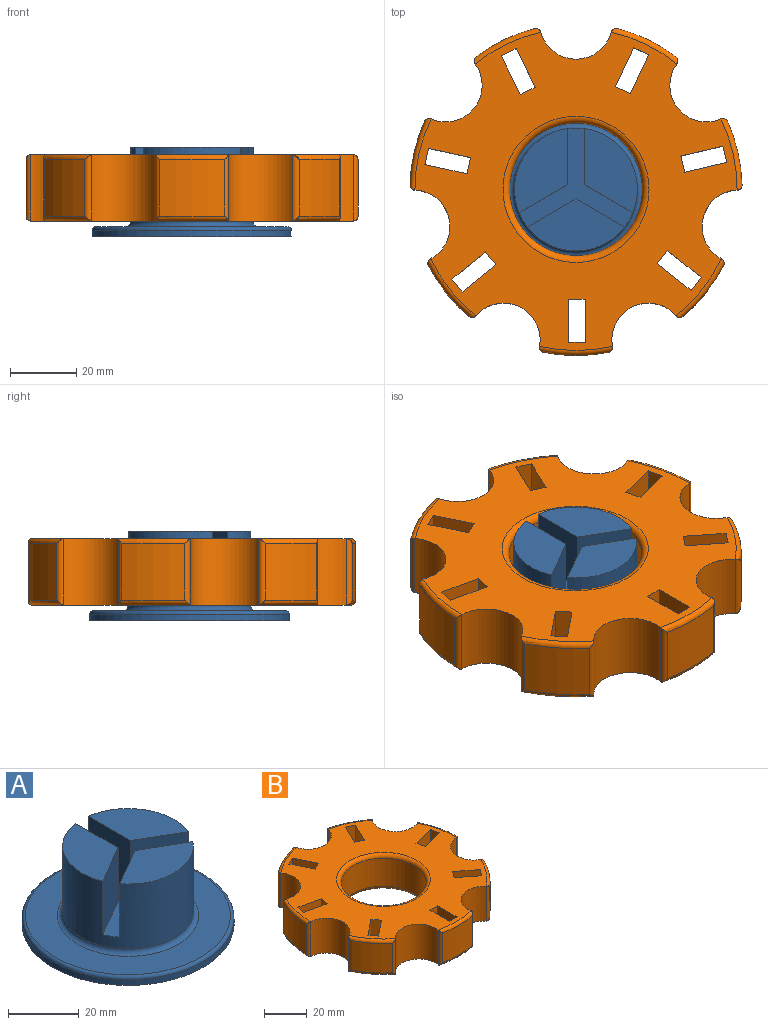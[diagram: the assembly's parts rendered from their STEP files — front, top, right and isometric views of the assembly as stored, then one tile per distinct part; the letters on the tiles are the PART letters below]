
ASSEMBLY  parts=2 mates=1
PART A: 16 faces, bbox 64.9x64.9x27 mm
  f0: plane 29.25x15.61mm, normal (0,0,1), area 269.8mm2, adj f3,f7,f8
  f1: plane 25.33x16mm, normal (0,0,1), area 269.8mm2, adj f3,f9,f10
  f2: plane 25.33x16mm, normal (0,0,1), area 269.8mm2, adj f3,f11,f12
  f3: cylinder r=18.5mm len=37mm, axis (0,0,-1), area 2337mm2, adj f0,f1,f2,f7,f8,f9,f10,f11
  f4: cylinder r=30mm len=60mm, axis (0,0,1), area 377mm2, adj f5,f15
  f5: plane 60x60mm, normal (0,0,-1), area 2827.4mm2, adj f4
  f6: plane 58x58mm, normal (0,0,1), area 1385.4mm2, adj f14,f15
  f7: plane 18.5x14.62mm, normal (-0.5,0.87,0), area 312.4mm2, adj f0,f3,f8,f13
  f8: plane 18.5x14.62mm, normal (0.5,0.87,0), area 312.4mm2, adj f0,f3,f7,f13
  f9: plane 18.5x14.62mm, normal (-0.5,-0.87,0), area 312.4mm2, adj f1,f3,f10,f13
  f10: plane 18.5x16.89mm, normal (-1,0,0), area 312.4mm2, adj f1,f3,f9,f13
  f11: plane 18.5x16.89mm, normal (1,0,0), area 312.4mm2, adj f2,f3,f12,f13
  f12: plane 18.5x14.62mm, normal (0.5,-0.87,0), area 312.4mm2, adj f2,f3,f11,f13
  f13: plane 34.25x29.83mm, normal (0,0,1), area 265.8mm2, adj f3,f7,f8,f9,f10,f11,f12
  f14: torus R=20mm, axis (0,0,-1), area 282mm2, adj f3,f6
  f15: torus R=29mm, axis (0,0,-1), area 292.5mm2, adj f4,f6
PART B: 75 faces, bbox 108.2x106.9x20 mm
  f0: cylinder r=50mm len=19.1mm, axis (0,0,-1), area 335.3mm2, adj f45,f46,f47,f48
  f1: cylinder r=50mm len=17.65mm, axis (0,0,-1), area 335.3mm2, adj f69,f70,f71,f72
  f2: cylinder r=50mm len=17mm, axis (0,0,-1), area 335.3mm2, adj f49,f50,f51,f52
  f3: cylinder r=50mm len=19.59mm, axis (0,0,-1), area 335.3mm2, adj f53,f54,f55,f56
  f4: cylinder r=50mm len=17mm, axis (0,0,-1), area 335.3mm2, adj f57,f58,f59,f60
  f5: cylinder r=50mm len=19.1mm, axis (0,0,-1), area 335.3mm2, adj f61,f62,f63,f64
  f6: cylinder r=50mm len=17.65mm, axis (0,0,-1), area 335.3mm2, adj f65,f66,f67,f68
  f7: plane 97x95.82mm, normal (0,0,1), area 4406.6mm2, adj f10,f11,f12,f13,f14,f15,f16,f17
  f8: plane 97x95.82mm, normal (0,0,-1), area 4406.6mm2, adj f10,f11,f12,f13,f14,f15,f16,f17
  f9: cylinder r=20mm len=40mm, axis (0,0,-1), area 2010.6mm2, adj f73,f74
  f10: plane 20x4.52mm, normal (-0.43,-0.9,0), area 100mm2, adj f7,f8,f11,f13
  f11: plane 20x11.75mm, normal (0.9,-0.43,0), area 260mm2, adj f7,f8,f10,f12
  f12: plane 20x4.52mm, normal (0.43,0.9,0), area 100mm2, adj f7,f8,f11,f13
  f13: plane 20x11.75mm, normal (-0.9,0.43,0), area 260mm2, adj f7,f8,f10,f12
  f14: plane 20x4.87mm, normal (-0.97,-0.23,0), area 100mm2, adj f7,f8,f15,f17
  f15: plane 20x12.65mm, normal (0.23,-0.97,0), area 260mm2, adj f7,f8,f14,f16
  f16: plane 20x4.87mm, normal (0.97,0.23,0), area 100mm2, adj f7,f8,f15,f17
  f17: plane 20x12.65mm, normal (-0.23,0.97,0), area 260mm2, adj f7,f8,f14,f16
  f18: plane 20x3.93mm, normal (-0.79,0.62,0), area 100mm2, adj f7,f8,f19,f21
  f19: plane 20x10.22mm, normal (-0.62,-0.79,0), area 260mm2, adj f7,f8,f18,f20
  f20: plane 20x3.93mm, normal (0.79,-0.62,0), area 100mm2, adj f7,f8,f19,f21
  f21: plane 20x10.22mm, normal (0.62,0.79,0), area 260mm2, adj f7,f8,f18,f20
  f22: plane 20x5mm, normal (-0.01,1,0), area 100mm2, adj f7,f8,f23,f25
  f23: plane 20x13mm, normal (-1,-0.01,0), area 260mm2, adj f7,f8,f22,f24
  f24: plane 20x5mm, normal (0.01,-1,0), area 100mm2, adj f7,f8,f23,f25
  f25: plane 20x13mm, normal (1,0.01,0), area 260mm2, adj f7,f8,f22,f24
  f26: plane 20x3.89mm, normal (0.78,0.63,0), area 100mm2, adj f7,f8,f27,f29
  f27: plane 20x10.11mm, normal (-0.63,0.78,0), area 260mm2, adj f7,f8,f26,f28
  f28: plane 20x3.89mm, normal (-0.78,-0.63,0), area 100mm2, adj f7,f8,f27,f29
  f29: plane 20x10.11mm, normal (0.63,-0.78,0), area 260mm2, adj f7,f8,f26,f28
  f30: plane 20x4.49mm, normal (-0.44,0.9,0), area 100mm2, adj f7,f8,f31,f33
  f31: plane 20x11.67mm, normal (-0.9,-0.44,0), area 260mm2, adj f7,f8,f30,f32
  f32: plane 20x4.49mm, normal (0.44,-0.9,0), area 100mm2, adj f7,f8,f31,f33
  f33: plane 20x11.67mm, normal (0.9,0.44,0), area 260mm2, adj f7,f8,f30,f32
  f34: plane 20x4.88mm, normal (0.98,-0.22,0), area 100mm2, adj f7,f8,f35,f37
  f35: plane 20x12.69mm, normal (0.22,0.98,0), area 260mm2, adj f7,f8,f34,f36
  f36: plane 20x4.88mm, normal (-0.98,0.22,0), area 100mm2, adj f7,f8,f35,f37
  f37: plane 20x12.69mm, normal (-0.22,-0.98,0), area 260mm2, adj f7,f8,f34,f36
  f38: cylinder r=11mm len=21.25mm, axis (0,0,-1), area 575.8mm2, adj f7,f8,f65,f66,f68,f69,f70,f71
  f39: cylinder r=11mm len=20mm, axis (0,0,-1), area 575.8mm2, adj f7,f8,f61,f62,f64,f65,f67,f68
  f40: cylinder r=11mm len=20.72mm, axis (0,0,-1), area 575.8mm2, adj f7,f8,f57,f58,f60,f61,f63,f64
  f41: cylinder r=11mm len=20mm, axis (0,0,-1), area 575.8mm2, adj f7,f8,f53,f54,f56,f57,f59,f60
  f42: cylinder r=11mm len=20mm, axis (0,0,-1), area 575.8mm2, adj f7,f8,f49,f50,f52,f53,f55,f56
  f43: cylinder r=11mm len=20.72mm, axis (0,0,-1), area 575.8mm2, adj f7,f8,f45,f46,f48,f49,f51,f52
  f44: cylinder r=11mm len=20mm, axis (0,0,-1), area 575.8mm2, adj f7,f8,f45,f47,f48,f70,f71,f72
  f45: torus R=48.5mm, axis (0,0,1), area 50.5mm2, adj f0,f8,f43,f44,f46,f47
  f46: cylinder r=1.5mm len=20mm, axis (0,0,-1), area 44.2mm2, adj f0,f43,f45,f48
  f47: cylinder r=1.5mm len=20mm, axis (0,0,1), area 44.2mm2, adj f0,f44,f45,f48
  f48: torus R=48.5mm, axis (0,0,1), area 50.5mm2, adj f0,f7,f43,f44,f46,f47
  f49: torus R=48.5mm, axis (0,0,1), area 50.5mm2, adj f2,f8,f42,f43,f50,f51
  f50: cylinder r=1.5mm len=20mm, axis (0,0,-1), area 44.2mm2, adj f2,f42,f49,f52
  f51: cylinder r=1.5mm len=20mm, axis (0,0,1), area 44.2mm2, adj f2,f43,f49,f52
  f52: torus R=48.5mm, axis (0,0,1), area 50.5mm2, adj f2,f7,f42,f43,f50,f51
  f53: torus R=48.5mm, axis (0,0,1), area 50.5mm2, adj f3,f8,f41,f42,f54,f55
  f54: cylinder r=1.5mm len=20mm, axis (0,0,-1), area 44.2mm2, adj f3,f41,f53,f56
  f55: cylinder r=1.5mm len=20mm, axis (0,0,1), area 44.2mm2, adj f3,f42,f53,f56
  f56: torus R=48.5mm, axis (0,0,1), area 50.5mm2, adj f3,f7,f41,f42,f54,f55
  f57: torus R=48.5mm, axis (0,0,1), area 50.5mm2, adj f4,f8,f40,f41,f58,f59
  f58: cylinder r=1.5mm len=20mm, axis (0,0,-1), area 44.2mm2, adj f4,f40,f57,f60
  f59: cylinder r=1.5mm len=20mm, axis (0,0,1), area 44.2mm2, adj f4,f41,f57,f60
  f60: torus R=48.5mm, axis (0,0,1), area 50.5mm2, adj f4,f7,f40,f41,f58,f59
  f61: torus R=48.5mm, axis (0,0,1), area 50.5mm2, adj f5,f8,f39,f40,f62,f63
  f62: cylinder r=1.5mm len=20mm, axis (0,0,-1), area 44.2mm2, adj f5,f39,f61,f64
  f63: cylinder r=1.5mm len=20mm, axis (0,0,1), area 44.2mm2, adj f5,f40,f61,f64
  f64: torus R=48.5mm, axis (0,0,1), area 50.5mm2, adj f5,f7,f39,f40,f62,f63
  f65: torus R=48.5mm, axis (0,0,1), area 50.5mm2, adj f6,f8,f38,f39,f66,f67
  f66: cylinder r=1.5mm len=20mm, axis (0,0,-1), area 44.2mm2, adj f6,f38,f65,f68
  f67: cylinder r=1.5mm len=20mm, axis (0,0,1), area 44.2mm2, adj f6,f39,f65,f68
  f68: torus R=48.5mm, axis (0,0,1), area 50.5mm2, adj f6,f7,f38,f39,f66,f67
  f69: cylinder r=1.5mm len=20mm, axis (0,0,1), area 44.2mm2, adj f1,f38,f70,f71
  f70: torus R=48.5mm, axis (0,0,1), area 50.5mm2, adj f1,f8,f38,f44,f69,f72
  f71: torus R=48.5mm, axis (0,0,1), area 50.5mm2, adj f1,f7,f38,f44,f69,f72
  f72: cylinder r=1.5mm len=20mm, axis (0,0,-1), area 44.2mm2, adj f1,f44,f70,f71
  f73: torus R=22mm, axis (0,0,1), area 409.1mm2, adj f7,f9
  f74: torus R=22mm, axis (0,0,1), area 409.1mm2, adj f8,f9
PLACE A t=(-83.59,-23.6,31.2)mm
PLACE B t=(-83.59,-23.6,32.95)mm
MATE revolute B.f9 <-> A.f3  axis (0,0,-1) through (-83.59,-23.6,34.95)mm
